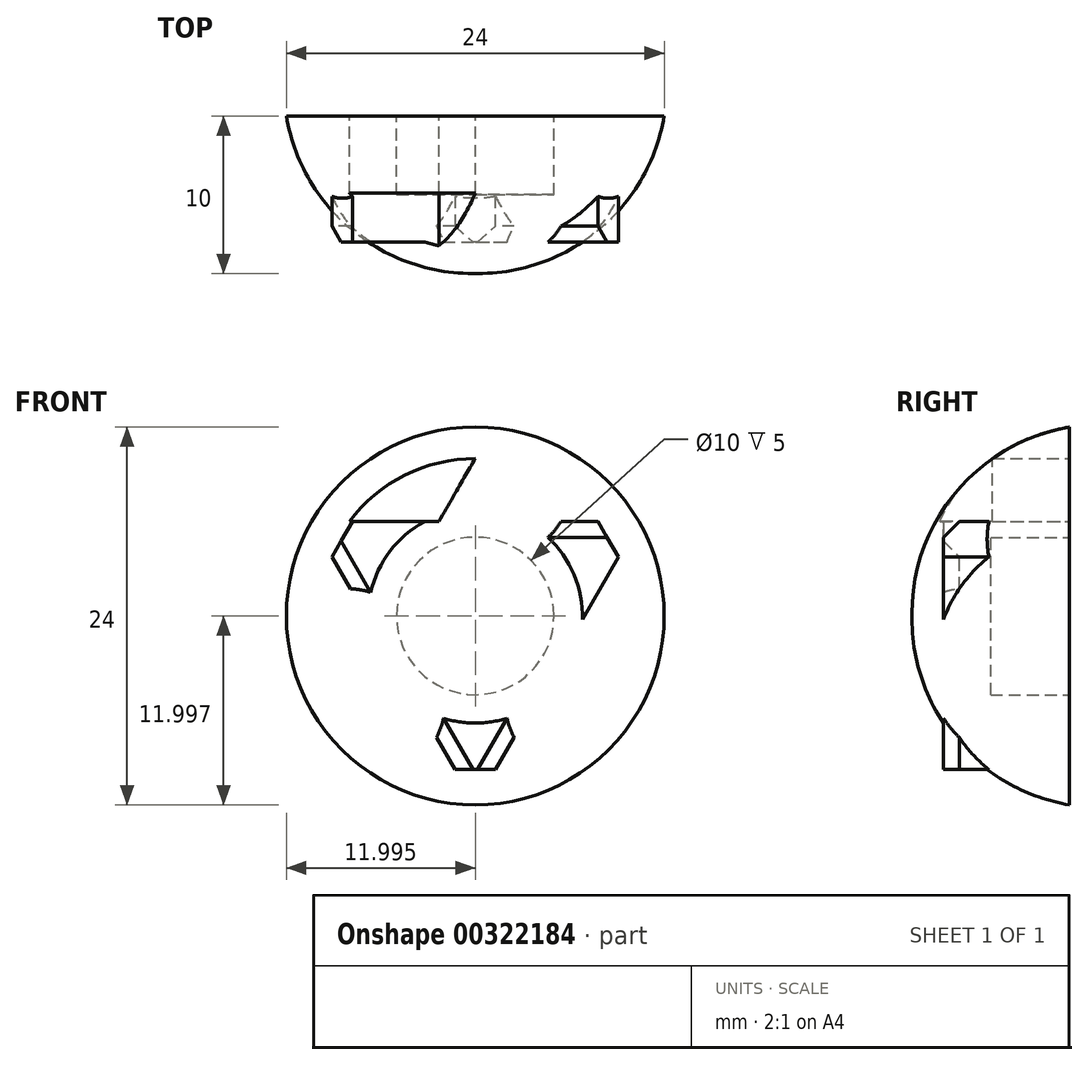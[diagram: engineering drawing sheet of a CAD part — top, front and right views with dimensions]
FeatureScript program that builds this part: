
annotation { "Feature Type Name" : "Feature", "Feature Type Description" : "" }
export const myFeature = defineFeature(function(context is Context, id is Id, definition is map)
    precondition{}
    {
        {
            var Q0;
            Q0=qCreatedBy(makeId("Front.planeOp"),FACE);
            var sketch = newSketch(context, id + "F0", { "sketchPlane" : qUnion([Q0])});
            skLineSegment(sketch, "E0", {"start": v(-12.34, 44) * mm, "end": v(-23.15, 37.75) * mm});
            skLineSegment(sketch, "E1", {"start": v(-23.15, 37.75) * mm, "end": v(-33.96, 44) * mm});
            skLineSegment(sketch, "E2", {"start": v(-33.96, 44) * mm, "end": v(-33.96, 56.47) * mm});
            skLineSegment(sketch, "E3", {"start": v(-33.96, 56.47) * mm, "end": v(-23.15, 62.71) * mm});
            skLineSegment(sketch, "E4", {"start": v(-23.15, 62.71) * mm, "end": v(-12.34, 56.47) * mm});
            skLineSegment(sketch, "E5", {"start": v(-12.34, 56.47) * mm, "end": v(-12.34, 44) * mm});
            skLineSegment(sketch, "E6", {"start": v(-12.34, 44) * mm, "end": v(-33.96, 44) * mm});
            skLineSegment(sketch, "E7", {"start": v(-33.96, 44) * mm, "end": v(-23.15, 62.71) * mm});
            skLineSegment(sketch, "E8", {"start": v(-23.15, 62.71) * mm, "end": v(-12.34, 44) * mm});
            skLineSegment(sketch, "E9", {"start": v(-23.15, 37.75) * mm, "end": v(-23.15, 62.71) * mm});
            skLineSegment(sketch, "E10", {"start": v(-12.34, 56.47) * mm, "end": v(-33.96, 44) * mm});
            skLineSegment(sketch, "E11", {"start": v(-12.34, 44) * mm, "end": v(-33.96, 56.47) * mm});
            skLineSegment(sketch, "E12", {"start": v(-23.15, 56.45) * mm, "end": v(-28.56, 53.35) * mm});
            skLineSegment(sketch, "E13", {"start": v(-28.56, 53.35) * mm, "end": v(-28.56, 47.13) * mm});
            skLineSegment(sketch, "E14", {"start": v(-28.56, 47.13) * mm, "end": v(-23.15, 44.02) * mm});
            skLineSegment(sketch, "E15", {"start": v(-23.15, 44.02) * mm, "end": v(-17.77, 47.13) * mm});
            skLineSegment(sketch, "E16", {"start": v(-17.77, 47.13) * mm, "end": v(-17.77, 53.34) * mm});
            skLineSegment(sketch, "E17", {"start": v(-17.77, 53.34) * mm, "end": v(-23.15, 56.45) * mm});
            skLineSegment(sketch, "E18", {"start": v(19.65, 43.9) * mm, "end": v(8.68, 37.56) * mm});
            skLineSegment(sketch, "E19", {"start": v(8.68, 37.56) * mm, "end": v(-2.3, 43.9) * mm});
            skLineSegment(sketch, "E20", {"start": v(-2.3, 43.9) * mm, "end": v(-2.3, 56.57) * mm});
            skLineSegment(sketch, "E21", {"start": v(-2.3, 56.57) * mm, "end": v(8.68, 62.9) * mm});
            skLineSegment(sketch, "E22", {"start": v(8.68, 62.9) * mm, "end": v(19.65, 56.57) * mm});
            skLineSegment(sketch, "E23", {"start": v(19.65, 56.57) * mm, "end": v(19.65, 43.9) * mm});
            skLineSegment(sketch, "E24", {"start": v(19.62, 56.59) * mm, "end": v(8.68, 37.64) * mm});
            skLineSegment(sketch, "E25", {"start": v(8.68, 37.64) * mm, "end": v(-2.26, 56.59) * mm});
            skLineSegment(sketch, "E26", {"start": v(-2.26, 56.59) * mm, "end": v(19.62, 56.59) * mm});
            skLineSegment(sketch, "E27", {"start": v(-0.37, 45.16) * mm, "end": v(8.68, 60.83) * mm});
            skLineSegment(sketch, "E28", {"start": v(8.68, 60.83) * mm, "end": v(17.73, 45.16) * mm});
            skLineSegment(sketch, "E29", {"start": v(17.73, 45.16) * mm, "end": v(-0.37, 45.16) * mm});
            skLineSegment(sketch, "E30", {"start": v(8.68, 37.64) * mm, "end": v(8.68, 50.35) * mm});
            skLineSegment(sketch, "E31", {"start": v(19.62, 56.59) * mm, "end": v(8.68, 50.35) * mm});
            skLineSegment(sketch, "E32", {"start": v(-2.26, 56.59) * mm, "end": v(8.68, 50.35) * mm});
            skLineSegment(sketch, "E33", {"start": v(-61.2, 39.46) * mm, "end": v(-54.99, 50.23) * mm});
            skLineSegment(sketch, "E34", {"start": v(-67.43, 50.23) * mm, "end": v(-54.99, 50.23) * mm});
            skLineSegment(sketch, "E35", {"start": v(-61.2, 39.46) * mm, "end": v(-67.43, 50.23) * mm});
            skLineSegment(sketch, "E36", {"start": v(-67.43, 50.23) * mm, "end": v(-61.2, 61) * mm});
            skLineSegment(sketch, "E37", {"start": v(-61.2, 61) * mm, "end": v(-48.77, 61) * mm});
            skLineSegment(sketch, "E38", {"start": v(-48.77, 61) * mm, "end": v(-42.54, 50.23) * mm});
            skLineSegment(sketch, "E39", {"start": v(-42.54, 50.23) * mm, "end": v(-48.77, 39.46) * mm});
            skLineSegment(sketch, "E40", {"start": v(-48.77, 39.46) * mm, "end": v(-61.2, 39.46) * mm});
            skLineSegment(sketch, "E41", {"start": v(-61.2, 61) * mm, "end": v(-54.99, 50.23) * mm});
            skLineSegment(sketch, "E42", {"start": v(-64.3, 44.87) * mm, "end": v(-54.99, 61) * mm});
            skLineSegment(sketch, "E43", {"start": v(-54.99, 61) * mm, "end": v(-45.67, 44.87) * mm});
            skLineSegment(sketch, "E44", {"start": v(-45.67, 44.87) * mm, "end": v(-64.3, 44.87) * mm});
            skLineSegment(sketch, "E45", {"start": v(-45.67, 55.6) * mm, "end": v(-54.99, 39.46) * mm});
            skLineSegment(sketch, "E46", {"start": v(-54.99, 39.46) * mm, "end": v(-64.3, 55.6) * mm});
            skLineSegment(sketch, "E47", {"start": v(-64.3, 55.6) * mm, "end": v(-45.67, 55.6) * mm});
            skLineSegment(sketch, "E48", {"start": v(-54.99, 50.23) * mm, "end": v(-54.99, 61) * mm});
            skLineSegment(sketch, "E49", {"start": v(-64.3, 44.87) * mm, "end": v(-54.99, 50.23) * mm});
            skLineSegment(sketch, "E50", {"start": v(-45.67, 44.87) * mm, "end": v(-54.99, 50.23) * mm});
            skLineSegment(sketch, "E51", {"start": v(-54.99, 61) * mm, "end": v(-64.3, 55.6) * mm});
            skLineSegment(sketch, "E52", {"start": v(-64.3, 55.6) * mm, "end": v(-64.3, 44.87) * mm});
            skLineSegment(sketch, "E53", {"start": v(-64.3, 44.87) * mm, "end": v(-54.99, 39.46) * mm});
            skLineSegment(sketch, "E54", {"start": v(-54.99, 39.46) * mm, "end": v(-45.67, 44.87) * mm});
            skLineSegment(sketch, "E55", {"start": v(-45.67, 44.87) * mm, "end": v(-45.67, 55.6) * mm});
            skLineSegment(sketch, "E56", {"start": v(-45.67, 55.6) * mm, "end": v(-54.99, 61) * mm});
            skLineSegment(sketch, "E57", {"start": v(-54.99, 50.23) * mm, "end": v(-45.67, 55.6) * mm});
            skLineSegment(sketch, "E58", {"start": v(-54.99, 39.46) * mm, "end": v(-54.99, 50.23) * mm});
            skLineSegment(sketch, "E59", {"start": v(-64.3, 55.6) * mm, "end": v(-54.99, 50.23) * mm});
            skLineSegment(sketch, "E60", {"start": v(-48.77, 39.46) * mm, "end": v(-54.99, 50.23) * mm});
            skLineSegment(sketch, "E61", {"start": v(-48.77, 60.99) * mm, "end": v(-54.99, 50.21) * mm});
            skLineSegment(sketch, "E62", {"start": v(-42.54, 50.21) * mm, "end": v(-54.99, 50.21) * mm});
            skCircle(sketch, "E63", {"center": v(-54.99, 50.21) * mm, "radius": 11.4 * mm});
            skCircle(sketch, "E64", {"center": v(-54.99, 50.23) * mm, "radius": 5.36 * mm});
            skCircle(sketch, "E65", {"center": v(-54.99, 50.21) * mm, "radius": 4.17 * mm});
            skCircle(sketch, "E66", {"center": v(-23.15, 50.23) * mm, "radius": 12.48 * mm});
            skCircle(sketch, "E67", {"center": v(-23.15, 50.23) * mm, "radius": 10.8 * mm});
            skCircle(sketch, "E68", {"center": v(-23.15, 50.23) * mm, "radius": 6.21 * mm});
            skCircle(sketch, "E69", {"center": v(-23.15, 50.23) * mm, "radius": 7.49 * mm});
            skCircle(sketch, "E70", {"center": v(8.68, 50.35) * mm, "radius": 10.44 * mm});
            skCircle(sketch, "E71", {"center": v(8.68, 50.35) * mm, "radius": 1.45 * mm});
            skCircle(sketch, "E72", {"center": v(8.68, 50.35) * mm, "radius": 5.24 * mm});
            skCircle(sketch, "E73", {"center": v(8.68, 50.35) * mm, "radius": 12.55 * mm});
            skSolve(sketch);
        }
        {
            var Q0;
            Q0=qCreatedBy(makeId("Front.planeOp"),FACE);
            var sketch = newSketch(context, id + "F1", { "sketchPlane" : qUnion([Q0])});
            skCircle(sketch, "E74", {"center": v(42.58, 50.35) * mm, "radius": 12 * mm});
            skCircle(sketch, "E75.cCircle", {"center": v(42.58, 50.35) * mm, "radius": 10.4 * mm, "construction": true});
            skLineSegment(sketch, "E75.0", {"start": v(42.58, 62.35) * mm, "end": v(52.97, 56.35) * mm});
            skLineSegment(sketch, "E75.1", {"start": v(52.97, 56.35) * mm, "end": v(52.97, 44.35) * mm});
            skLineSegment(sketch, "E75.2", {"start": v(52.97, 44.35) * mm, "end": v(42.58, 38.35) * mm});
            skLineSegment(sketch, "E75.3", {"start": v(42.58, 38.35) * mm, "end": v(32.18, 44.35) * mm});
            skLineSegment(sketch, "E75.4", {"start": v(32.18, 44.35) * mm, "end": v(32.18, 56.35) * mm});
            skLineSegment(sketch, "E75.5", {"start": v(32.18, 56.35) * mm, "end": v(42.58, 62.35) * mm});
            skPoint(sketch, "E75.0.midPoint", {"position": v(47.77, 59.35) * mm});
            skCircle(sketch, "E76.cCircle", {"center": v(42.58, 50.35) * mm, "radius": 6 * mm, "construction": true});
            skLineSegment(sketch, "E76.0", {"start": v(52.97, 56.35) * mm, "end": v(42.58, 38.35) * mm});
            skLineSegment(sketch, "E76.1", {"start": v(42.58, 38.35) * mm, "end": v(32.18, 56.35) * mm});
            skLineSegment(sketch, "E76.2", {"start": v(32.18, 56.35) * mm, "end": v(52.97, 56.35) * mm});
            skPoint(sketch, "E76.0.midPoint", {"position": v(47.77, 47.35) * mm});
            skCircle(sketch, "E77", {"center": v(42.58, 50.35) * mm, "radius": 10 * mm});
            skCircle(sketch, "E78.cCircle", {"center": v(42.58, 50.35) * mm, "radius": 5 * mm, "construction": true});
            skLineSegment(sketch, "E78.0", {"start": v(42.58, 60.35) * mm, "end": v(51.24, 45.35) * mm});
            skLineSegment(sketch, "E78.1", {"start": v(51.24, 45.35) * mm, "end": v(33.91, 45.35) * mm});
            skLineSegment(sketch, "E78.2", {"start": v(33.91, 45.35) * mm, "end": v(42.58, 60.35) * mm});
            skPoint(sketch, "E78.0.midPoint", {"position": v(46.9, 52.85) * mm});
            skCircle(sketch, "E79", {"center": v(42.58, 50.35) * mm, "radius": 5 * mm});
            skSolve(sketch);
        }
        {
            var Q0;
            {var subQ0=sQuery(id+"F1.wireOp",EDGE,"E75.5");Q0=makeQuery(id+"F1.imprint","IMPRINT",FACE,{"disambiguationData":[TD([[makeQuery(id+"F1.imprint","IMPRINT",EDGE,{"derivedFrom":subQ0}),1.0]])]});}
            var Q1;
            {var subQ0=sQuery(id+"F1.wireOp",EDGE,"E75.4");Q1=makeQuery(id+"F1.imprint","IMPRINT",FACE,{"disambiguationData":[TD([[makeQuery(id+"F1.imprint","IMPRINT",EDGE,{"derivedFrom":subQ0}),1.0]])]});}
            var Q2;
            {var subQ0=sQuery(id+"F1.wireOp",EDGE,"E75.3");Q2=makeQuery(id+"F1.imprint","IMPRINT",FACE,{"disambiguationData":[TD([[makeQuery(id+"F1.imprint","IMPRINT",EDGE,{"derivedFrom":subQ0}),1.0]])]});}
            var Q3;
            {var subQ0=sQuery(id+"F1.wireOp",EDGE,"E75.2");Q3=makeQuery(id+"F1.imprint","IMPRINT",FACE,{"disambiguationData":[TD([[makeQuery(id+"F1.imprint","IMPRINT",EDGE,{"derivedFrom":subQ0}),1.0]])]});}
            var Q4;
            {var subQ0=sQuery(id+"F1.wireOp",EDGE,"E75.1");Q4=makeQuery(id+"F1.imprint","IMPRINT",FACE,{"disambiguationData":[TD([[makeQuery(id+"F1.imprint","IMPRINT",EDGE,{"derivedFrom":subQ0}),1.0]])]});}
            var Q5;
            {var subQ0=sQuery(id+"F1.wireOp",EDGE,"E75.0");Q5=makeQuery(id+"F1.imprint","IMPRINT",FACE,{"disambiguationData":[TD([[makeQuery(id+"F1.imprint","IMPRINT",EDGE,{"derivedFrom":subQ0}),1.0]])]});}
            var Q6;
            {var subQ7=sQuery(id+"F1.wireOp",EDGE,"E75.3");Q6=makeQuery(id+"F1.imprint","IMPRINT",FACE,{"disambiguationData":[TD([[makeQuery(id+"F1.imprint","IMPRINT",EDGE,{"derivedFrom":subQ7}),-1.0]])]});}
            var Q7;
            {var subQ0=sQuery(id+"F1.wireOp",EDGE,"E78.2");var subQ1=sQuery(id+"F1.wireOp",EDGE,"E76.1");var subQ2=makeQuery(id+"F1.imprint","INTERSECT",VERTEX,{"derivedFrom":[subQ1,subQ0]});Q7=makeQuery(id+"F1.imprint","IMPRINT",FACE,{"disambiguationData":[TD([[makeQuery(id+"F1.imprint","IMPRINT",EDGE,{"disambiguationData":[TD([[subQ2,-1.0]])],"derivedFrom":subQ1}),1.0]])]});}
            var Q8;
            {var subQ0=sQuery(id+"F1.wireOp",EDGE,"E78.1");var subQ1=sQuery(id+"F1.wireOp",EDGE,"E76.1");var subQ2=makeQuery(id+"F1.imprint","INTERSECT",VERTEX,{"derivedFrom":[subQ1,subQ0]});Q8=makeQuery(id+"F1.imprint","IMPRINT",FACE,{"disambiguationData":[TD([[makeQuery(id+"F1.imprint","IMPRINT",EDGE,{"disambiguationData":[TD([[subQ2,-1.0]])],"derivedFrom":subQ1}),1.0]])]});}
            var Q9;
            {var subQ0=sQuery(id+"F1.wireOp",EDGE,"E77");var subQ1=sQuery(id+"F1.wireOp",EDGE,"E76.1");var subQ2=makeQuery(id+"F1.imprint","INTERSECT",VERTEX,{"disambiguationData":[OD(0.0)],"derivedFrom":[subQ1,subQ0]});Q9=makeQuery(id+"F1.imprint","IMPRINT",FACE,{"disambiguationData":[TD([[makeQuery(id+"F1.imprint","IMPRINT",EDGE,{"disambiguationData":[TD([[subQ2,-1.0]])],"derivedFrom":subQ1}),1.0]])]});}
            var Q10;
            {var subQ0=sQuery(id+"F1.wireOp",EDGE,"E78.0");var subQ1=sQuery(id+"F1.wireOp",EDGE,"E76.0");var subQ2=makeQuery(id+"F1.imprint","INTERSECT",VERTEX,{"derivedFrom":[subQ1,subQ0]});Q10=makeQuery(id+"F1.imprint","IMPRINT",FACE,{"disambiguationData":[TD([[makeQuery(id+"F1.imprint","IMPRINT",EDGE,{"disambiguationData":[TD([[subQ2,-1.0]])],"derivedFrom":subQ1}),1.0]])]});}
            var Q11;
            {var subQ0=sQuery(id+"F1.wireOp",EDGE,"E79");var subQ1=makeQuery(id+"F1.imprint","INTERSECT",VERTEX,{"derivedFrom":[sQuery(id+"F1.wireOp",EDGE,"E78.0"),subQ0]});Q11=makeQuery(id+"F1.imprint","IMPRINT",FACE,{"disambiguationData":[TD([[makeQuery(id+"F1.imprint","IMPRINT",EDGE,{"disambiguationData":[TD([[subQ1,-1.0]])],"derivedFrom":subQ0}),1.0]])]});}
            var Q12;
            {var subQ0=sQuery(id+"F1.wireOp",EDGE,"E78.0");var subQ1=sQuery(id+"F1.wireOp",EDGE,"E76.2");var subQ2=makeQuery(id+"F1.imprint","INTERSECT",VERTEX,{"derivedFrom":[subQ1,subQ0]});Q12=makeQuery(id+"F1.imprint","IMPRINT",FACE,{"disambiguationData":[TD([[makeQuery(id+"F1.imprint","IMPRINT",EDGE,{"disambiguationData":[TD([[subQ2,-1.0]])],"derivedFrom":subQ1}),1.0]])]});}
            var Q13;
            {var subQ0=sQuery(id+"F1.wireOp",EDGE,"E78.1");var subQ1=sQuery(id+"F1.wireOp",EDGE,"E76.0");var subQ2=makeQuery(id+"F1.imprint","INTERSECT",VERTEX,{"derivedFrom":[subQ1,subQ0]});Q13=makeQuery(id+"F1.imprint","IMPRINT",FACE,{"disambiguationData":[TD([[makeQuery(id+"F1.imprint","IMPRINT",EDGE,{"disambiguationData":[TD([[subQ2,-1.0]])],"derivedFrom":subQ1}),1.0]])]});}
            var Q14;
            {var subQ0=sQuery(id+"F1.wireOp",EDGE,"E78.0");var subQ1=sQuery(id+"F1.wireOp",EDGE,"E76.0");var subQ2=makeQuery(id+"F1.imprint","INTERSECT",VERTEX,{"derivedFrom":[subQ1,subQ0]});Q14=makeQuery(id+"F1.imprint","IMPRINT",FACE,{"disambiguationData":[TD([[makeQuery(id+"F1.imprint","IMPRINT",EDGE,{"disambiguationData":[TD([[subQ2,-1.0]])],"derivedFrom":subQ1}),-1.0]])]});}
            var Q15;
            {var subQ4=sQuery(id+"F1.wireOp",EDGE,"E77");var subQ5=sQuery(id+"F1.wireOp",EDGE,"E76.0");var subQ6=makeQuery(id+"F1.imprint","INTERSECT",VERTEX,{"disambiguationData":[OD(0.0)],"derivedFrom":[subQ5,subQ4]});Q15=makeQuery(id+"F1.imprint","IMPRINT",FACE,{"disambiguationData":[TD([[makeQuery(id+"F1.imprint","IMPRINT",EDGE,{"disambiguationData":[TD([[subQ6,-1.0]])],"derivedFrom":subQ5}),-1.0]])]});}
            var Q16;
            {var subQ0=sQuery(id+"F1.wireOp",EDGE,"E78.1");var subQ1=sQuery(id+"F1.wireOp",EDGE,"E76.1");var subQ2=makeQuery(id+"F1.imprint","INTERSECT",VERTEX,{"derivedFrom":[subQ1,subQ0]});Q16=makeQuery(id+"F1.imprint","IMPRINT",FACE,{"disambiguationData":[TD([[makeQuery(id+"F1.imprint","IMPRINT",EDGE,{"disambiguationData":[TD([[subQ2,-1.0]])],"derivedFrom":subQ1}),-1.0]])]});}
            var Q17;
            {var subQ0=sQuery(id+"F1.wireOp",EDGE,"E78.2");var subQ1=sQuery(id+"F1.wireOp",EDGE,"E76.2");var subQ2=makeQuery(id+"F1.imprint","INTERSECT",VERTEX,{"derivedFrom":[subQ1,subQ0]});Q17=makeQuery(id+"F1.imprint","IMPRINT",FACE,{"disambiguationData":[TD([[makeQuery(id+"F1.imprint","IMPRINT",EDGE,{"disambiguationData":[TD([[subQ2,-1.0]])],"derivedFrom":subQ1}),-1.0]])]});}
            var Q18;
            {var subQ0=sQuery(id+"F1.wireOp",EDGE,"E78.1");var subQ1=sQuery(id+"F1.wireOp",EDGE,"E76.0");var subQ2=makeQuery(id+"F1.imprint","INTERSECT",VERTEX,{"derivedFrom":[subQ1,subQ0]});Q18=makeQuery(id+"F1.imprint","IMPRINT",FACE,{"disambiguationData":[TD([[makeQuery(id+"F1.imprint","IMPRINT",EDGE,{"disambiguationData":[TD([[subQ2,-1.0]])],"derivedFrom":subQ1}),-1.0]])]});}
            var Q19;
            {var subQ0=sQuery(id+"F1.wireOp",EDGE,"E78.2");var subQ1=sQuery(id+"F1.wireOp",EDGE,"E76.2");var subQ2=makeQuery(id+"F1.imprint","INTERSECT",VERTEX,{"derivedFrom":[subQ1,subQ0]});Q19=makeQuery(id+"F1.imprint","IMPRINT",FACE,{"disambiguationData":[TD([[makeQuery(id+"F1.imprint","IMPRINT",EDGE,{"disambiguationData":[TD([[subQ2,-1.0]])],"derivedFrom":subQ1}),1.0]])]});}
            var Q20;
            {var subQ1=sQuery(id+"F1.wireOp",EDGE,"E76.0");var subQ3=sQuery(id+"F1.wireOp",EDGE,"E77");var subQ4=makeQuery(id+"F1.imprint","INTERSECT",VERTEX,{"disambiguationData":[OD(0.0)],"derivedFrom":[subQ1,subQ3]});Q20=makeQuery(id+"F1.imprint","IMPRINT",FACE,{"disambiguationData":[TD([[makeQuery(id+"F1.imprint","IMPRINT",EDGE,{"disambiguationData":[TD([[subQ4,-1.0]])],"derivedFrom":subQ3}),-1.0]])]});}
            var Q21;
            {var subQ5=sQuery(id+"F1.wireOp",EDGE,"E75.0");Q21=makeQuery(id+"F1.imprint","IMPRINT",FACE,{"disambiguationData":[TD([[makeQuery(id+"F1.imprint","IMPRINT",EDGE,{"derivedFrom":subQ5}),-1.0]])]});}
            var Q22;
            {var subQ1=sQuery(id+"F1.wireOp",EDGE,"E76.1");var subQ3=sQuery(id+"F1.wireOp",EDGE,"E77");var subQ4=makeQuery(id+"F1.imprint","INTERSECT",VERTEX,{"disambiguationData":[OD(1.0)],"derivedFrom":[subQ1,subQ3]});Q22=makeQuery(id+"F1.imprint","IMPRINT",FACE,{"disambiguationData":[TD([[makeQuery(id+"F1.imprint","IMPRINT",EDGE,{"disambiguationData":[TD([[subQ4,1.0]])],"derivedFrom":subQ3}),-1.0]])]});}
            var Q23;
            {var subQ0=sQuery(id+"F1.wireOp",EDGE,"E77");var subQ1=sQuery(id+"F1.wireOp",EDGE,"E76.0");var subQ2=makeQuery(id+"F1.imprint","INTERSECT",VERTEX,{"disambiguationData":[OD(0.0)],"derivedFrom":[subQ1,subQ0]});Q23=makeQuery(id+"F1.imprint","IMPRINT",FACE,{"disambiguationData":[TD([[makeQuery(id+"F1.imprint","IMPRINT",EDGE,{"disambiguationData":[TD([[subQ2,-1.0]])],"derivedFrom":subQ1}),1.0]])]});}
            var Q24;
            {var subQ5=sQuery(id+"F1.wireOp",EDGE,"E75.1");Q24=makeQuery(id+"F1.imprint","IMPRINT",FACE,{"disambiguationData":[TD([[makeQuery(id+"F1.imprint","IMPRINT",EDGE,{"derivedFrom":subQ5}),-1.0]])]});}
            var Q25;
            {var subQ1=sQuery(id+"F1.wireOp",EDGE,"E76.0");var subQ3=sQuery(id+"F1.wireOp",EDGE,"E77");var subQ4=makeQuery(id+"F1.imprint","INTERSECT",VERTEX,{"disambiguationData":[OD(1.0)],"derivedFrom":[subQ1,subQ3]});Q25=makeQuery(id+"F1.imprint","IMPRINT",FACE,{"disambiguationData":[TD([[makeQuery(id+"F1.imprint","IMPRINT",EDGE,{"disambiguationData":[TD([[subQ4,1.0]])],"derivedFrom":subQ3}),-1.0]])]});}
            var Q26;
            {var subQ3=sQuery(id+"F1.wireOp",EDGE,"E78.2");var subQ5=sQuery(id+"F1.wireOp",EDGE,"E76.1");var subQ6=makeQuery(id+"F1.imprint","INTERSECT",VERTEX,{"derivedFrom":[subQ5,subQ3]});Q26=makeQuery(id+"F1.imprint","IMPRINT",FACE,{"disambiguationData":[TD([[makeQuery(id+"F1.imprint","IMPRINT",EDGE,{"disambiguationData":[TD([[subQ6,-1.0]])],"derivedFrom":subQ5}),-1.0]])]});}
            var Q27;
            {var subQ0=sQuery(id+"F1.wireOp",EDGE,"E77");var subQ1=sQuery(id+"F1.wireOp",EDGE,"E76.2");var subQ2=makeQuery(id+"F1.imprint","INTERSECT",VERTEX,{"disambiguationData":[OD(0.0)],"derivedFrom":[subQ1,subQ0]});Q27=makeQuery(id+"F1.imprint","IMPRINT",FACE,{"disambiguationData":[TD([[makeQuery(id+"F1.imprint","IMPRINT",EDGE,{"disambiguationData":[TD([[subQ2,-1.0]])],"derivedFrom":subQ1}),1.0]])]});}
            extrude(context, id + "F2", {"entities" : qUnion([Q0, Q1, Q2, Q3, Q4, Q5, Q6, Q7, Q8, Q9, Q10, Q11, Q12, Q13, Q14, Q15, Q16, Q17, Q18, Q19, Q20, Q21, Q22, Q23, Q24, Q25, Q26, Q27]), "depth" : 10 * mm});
        }
        {
            var Q0;
            Q0=makeQuery(id+"F2.opExtrude","CAP_EDGE",EDGE,{"disambiguationData":[OSD([sQuery(id+"F1.wireOp",EDGE,"E74")])],"isStart":false});
            fillet(context, id + "F3", {"entities" : qUnion([Q0]), "radius" : 12 * mm, "tangentPropagation" : true, "allowEdgeOverflow" : false});
        }
        {
            var Q0;
            {var subQ3=sQuery(id+"F1.wireOp",EDGE,"E78.2");var subQ5=sQuery(id+"F1.wireOp",EDGE,"E76.1");var subQ6=makeQuery(id+"F1.imprint","INTERSECT",VERTEX,{"derivedFrom":[subQ5,subQ3]});Q0=makeQuery(id+"F1.imprint","IMPRINT",FACE,{"disambiguationData":[TD([[makeQuery(id+"F1.imprint","IMPRINT",EDGE,{"disambiguationData":[TD([[subQ6,-1.0]])],"derivedFrom":subQ5}),-1.0]])]});}
            var Q1;
            {var subQ1=sQuery(id+"F1.wireOp",EDGE,"E76.1");var subQ3=sQuery(id+"F1.wireOp",EDGE,"E77");var subQ4=makeQuery(id+"F1.imprint","INTERSECT",VERTEX,{"disambiguationData":[OD(1.0)],"derivedFrom":[subQ1,subQ3]});Q1=makeQuery(id+"F1.imprint","IMPRINT",FACE,{"disambiguationData":[TD([[makeQuery(id+"F1.imprint","IMPRINT",EDGE,{"disambiguationData":[TD([[subQ4,1.0]])],"derivedFrom":subQ3}),-1.0]])]});}
            var Q2;
            {var subQ4=sQuery(id+"F1.wireOp",EDGE,"E77");var subQ5=sQuery(id+"F1.wireOp",EDGE,"E76.0");var subQ6=makeQuery(id+"F1.imprint","INTERSECT",VERTEX,{"disambiguationData":[OD(0.0)],"derivedFrom":[subQ5,subQ4]});Q2=makeQuery(id+"F1.imprint","IMPRINT",FACE,{"disambiguationData":[TD([[makeQuery(id+"F1.imprint","IMPRINT",EDGE,{"disambiguationData":[TD([[subQ6,-1.0]])],"derivedFrom":subQ5}),-1.0]])]});}
            var Q3;
            {var subQ1=sQuery(id+"F1.wireOp",EDGE,"E76.0");var subQ3=sQuery(id+"F1.wireOp",EDGE,"E77");var subQ4=makeQuery(id+"F1.imprint","INTERSECT",VERTEX,{"disambiguationData":[OD(0.0)],"derivedFrom":[subQ1,subQ3]});Q3=makeQuery(id+"F1.imprint","IMPRINT",FACE,{"disambiguationData":[TD([[makeQuery(id+"F1.imprint","IMPRINT",EDGE,{"disambiguationData":[TD([[subQ4,-1.0]])],"derivedFrom":subQ3}),-1.0]])]});}
            var Q4;
            {var subQ0=sQuery(id+"F1.wireOp",EDGE,"E78.1");var subQ1=sQuery(id+"F1.wireOp",EDGE,"E76.0");var subQ2=makeQuery(id+"F1.imprint","INTERSECT",VERTEX,{"derivedFrom":[subQ1,subQ0]});Q4=makeQuery(id+"F1.imprint","IMPRINT",FACE,{"disambiguationData":[TD([[makeQuery(id+"F1.imprint","IMPRINT",EDGE,{"disambiguationData":[TD([[subQ2,-1.0]])],"derivedFrom":subQ1}),-1.0]])]});}
            var Q5;
            {var subQ1=sQuery(id+"F1.wireOp",EDGE,"E76.0");var subQ3=sQuery(id+"F1.wireOp",EDGE,"E77");var subQ4=makeQuery(id+"F1.imprint","INTERSECT",VERTEX,{"disambiguationData":[OD(1.0)],"derivedFrom":[subQ1,subQ3]});Q5=makeQuery(id+"F1.imprint","IMPRINT",FACE,{"disambiguationData":[TD([[makeQuery(id+"F1.imprint","IMPRINT",EDGE,{"disambiguationData":[TD([[subQ4,1.0]])],"derivedFrom":subQ3}),-1.0]])]});}
            extrude(context, id + "F4", {"entities" : qUnion([Q0, Q1, Q2, Q3, Q4, Q5]), "operationType" : NewBodyOperationType.ADD, "depth" : 8 * mm});
        }
        {
            var Q0;
            {var subQ0=sQuery(id+"F1.wireOp",EDGE,"E79");var subQ1=makeQuery(id+"F1.imprint","INTERSECT",VERTEX,{"derivedFrom":[sQuery(id+"F1.wireOp",EDGE,"E78.0"),subQ0]});Q0=makeQuery(id+"F1.imprint","IMPRINT",FACE,{"disambiguationData":[TD([[makeQuery(id+"F1.imprint","IMPRINT",EDGE,{"disambiguationData":[TD([[subQ1,-1.0]])],"derivedFrom":subQ0}),1.0]])]});}
            extrude(context, id + "F5", {"entities" : qUnion([Q0]), "operationType" : NewBodyOperationType.REMOVE, "depth" : 5 * mm, "hasSecondDirection" : true, "secondDirectionOppositeDirection" : true, "secondDirectionDepth" : 25 * mm});
        }
        {
            var Q0;
            {var subQ0=sQuery(id+"F1.wireOp",EDGE,"E76.1");var subQ1=makeQuery(id+"F1.imprint","INTERSECT",VERTEX,{"disambiguationData":[OD(1.0)],"derivedFrom":[subQ0,sQuery(id+"F1.wireOp",EDGE,"E77")]});Q0=makeQuery(id+"F4.opExtrude","CAP_EDGE",EDGE,{"disambiguationData":[OSD([subQ0]),TDD([makeQuery(id+"F1.imprint","IMPRINT",EDGE,{"disambiguationData":[TD([[makeQuery(id+"F1.imprint","INTERSECT",VERTEX,{"derivedFrom":[subQ0,sQuery(id+"F1.wireOp",EDGE,"E78.2")]}),-1.0]])],"derivedFrom":subQ0}),makeQuery(id+"F1.imprint","IMPRINT",EDGE,{"disambiguationData":[TD([[subQ1,-1.0]])],"derivedFrom":subQ0})])],"isStart":false});}
            var Q1;
            {var subQ0=sQuery(id+"F1.wireOp",EDGE,"E76.2");var subQ1=makeQuery(id+"F1.imprint","INTERSECT",VERTEX,{"disambiguationData":[OD(0.0)],"derivedFrom":[subQ0,sQuery(id+"F1.wireOp",EDGE,"E77")]});Q1=makeQuery(id+"F4.opExtrude","CAP_EDGE",EDGE,{"disambiguationData":[OSD([subQ0]),TDD([makeQuery(id+"F1.imprint","IMPRINT",EDGE,{"disambiguationData":[TD([[subQ1,1.0]])],"derivedFrom":subQ0}),makeQuery(id+"F1.imprint","IMPRINT",EDGE,{"disambiguationData":[TD([[subQ1,-1.0]])],"derivedFrom":subQ0})])],"isStart":false});}
            var Q2;
            {var subQ0=sQuery(id+"F1.wireOp",EDGE,"E76.1");var subQ1=makeQuery(id+"F1.imprint","INTERSECT",VERTEX,{"disambiguationData":[OD(0.0)],"derivedFrom":[subQ0,sQuery(id+"F1.wireOp",EDGE,"E77")]});Q2=makeQuery(id+"F4.opExtrude","CAP_EDGE",EDGE,{"disambiguationData":[OSD([subQ0]),TDD([makeQuery(id+"F1.imprint","IMPRINT",EDGE,{"disambiguationData":[TD([[subQ1,1.0]])],"derivedFrom":subQ0}),makeQuery(id+"F1.imprint","IMPRINT",EDGE,{"disambiguationData":[TD([[subQ1,-1.0]])],"derivedFrom":subQ0})])],"isStart":false});}
            var Q3;
            {var subQ0=sQuery(id+"F1.wireOp",EDGE,"E76.0");var subQ1=makeQuery(id+"F1.imprint","INTERSECT",VERTEX,{"disambiguationData":[OD(1.0)],"derivedFrom":[subQ0,sQuery(id+"F1.wireOp",EDGE,"E77")]});Q3=makeQuery(id+"F4.opExtrude","CAP_EDGE",EDGE,{"disambiguationData":[OSD([subQ0]),TDD([makeQuery(id+"F1.imprint","IMPRINT",EDGE,{"disambiguationData":[TD([[makeQuery(id+"F1.imprint","INTERSECT",VERTEX,{"derivedFrom":[subQ0,sQuery(id+"F1.wireOp",EDGE,"E78.1")]}),-1.0]])],"derivedFrom":subQ0}),makeQuery(id+"F1.imprint","IMPRINT",EDGE,{"disambiguationData":[TD([[subQ1,-1.0]])],"derivedFrom":subQ0})])],"isStart":false});}
            chamfer(context, id + "F6", {"entities" : qUnion([Q0, Q1, Q2, Q3]), "width" : 1 * mm, "tangentPropagation" : true});
        }
        {
            var Q0;
            Q0=makeQuery(id+"F4.opExtrude","SWEPT_EDGE",EDGE,{"disambiguationData":[OSD([sQuery(id+"F1.wireOp",EDGE,"E74"),sQuery(id+"F1.wireOp",EDGE,"E75.4"),sQuery(id+"F1.wireOp",EDGE,"E75.5"),sQuery(id+"F1.wireOp",EDGE,"E76.1"),sQuery(id+"F1.wireOp",EDGE,"E76.2")])]});
            var Q1;
            Q1=makeQuery(id+"F4.opExtrude","SWEPT_EDGE",EDGE,{"disambiguationData":[OSD([sQuery(id+"F1.wireOp",EDGE,"E74"),sQuery(id+"F1.wireOp",EDGE,"E75.2"),sQuery(id+"F1.wireOp",EDGE,"E75.3"),sQuery(id+"F1.wireOp",EDGE,"E76.0"),sQuery(id+"F1.wireOp",EDGE,"E76.1")])]});
            var Q2;
            Q2=makeQuery(id+"F4.opExtrude","SWEPT_EDGE",EDGE,{"disambiguationData":[OSD([sQuery(id+"F1.wireOp",EDGE,"E74"),sQuery(id+"F1.wireOp",EDGE,"E75.0"),sQuery(id+"F1.wireOp",EDGE,"E75.1"),sQuery(id+"F1.wireOp",EDGE,"E76.0"),sQuery(id+"F1.wireOp",EDGE,"E76.2")])]});
            chamfer(context, id + "F7", {"entities" : qUnion([Q0, Q1, Q2]), "width" : 1.5 * mm, "tangentPropagation" : true});
        }
    });
